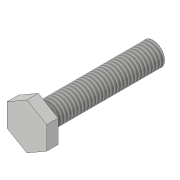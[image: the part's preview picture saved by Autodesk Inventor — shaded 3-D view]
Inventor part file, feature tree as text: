
AUTODESK INVENTOR PART (.ipt)
format: ipt  version: 2018.3 (Build 223284000, 284)  size: 90,624 bytes
history: native  units: in
note: dims shown in document units (in); Inventor stores cm internally (conversion verified against a paired STEP export)
features: extrude x2, sketch x2, thread x1
ambient origin geometry x8: Origin, YZ Plane, XZ Plane, XY Plane, X Axis, Y Axis, Z Axis, Center Point
bodies: Solid1 (feature_tree)
feature tree (5):
  extrude  "Extrusion1"  Depth=0.5in
  extrude  "Extrusion2"  Depth=2.5in TaperAngle=0.0deg
  thread  "Thread1"  [1 undecoded]
  sketch  "Sketch1"  dims[d0=0.25in d1=0.0in d2=0.5in]
  sketch  "Sketch2"  dims[d3=1.0in d4=2.5in d5=0.0in d6=1.0in d7=0.0in]
note: 1 required parameter value undecoded (feature->parameter linkage not recoverable at this tier; creation-order binding heuristic only, values carry confidence <= 0.55)
